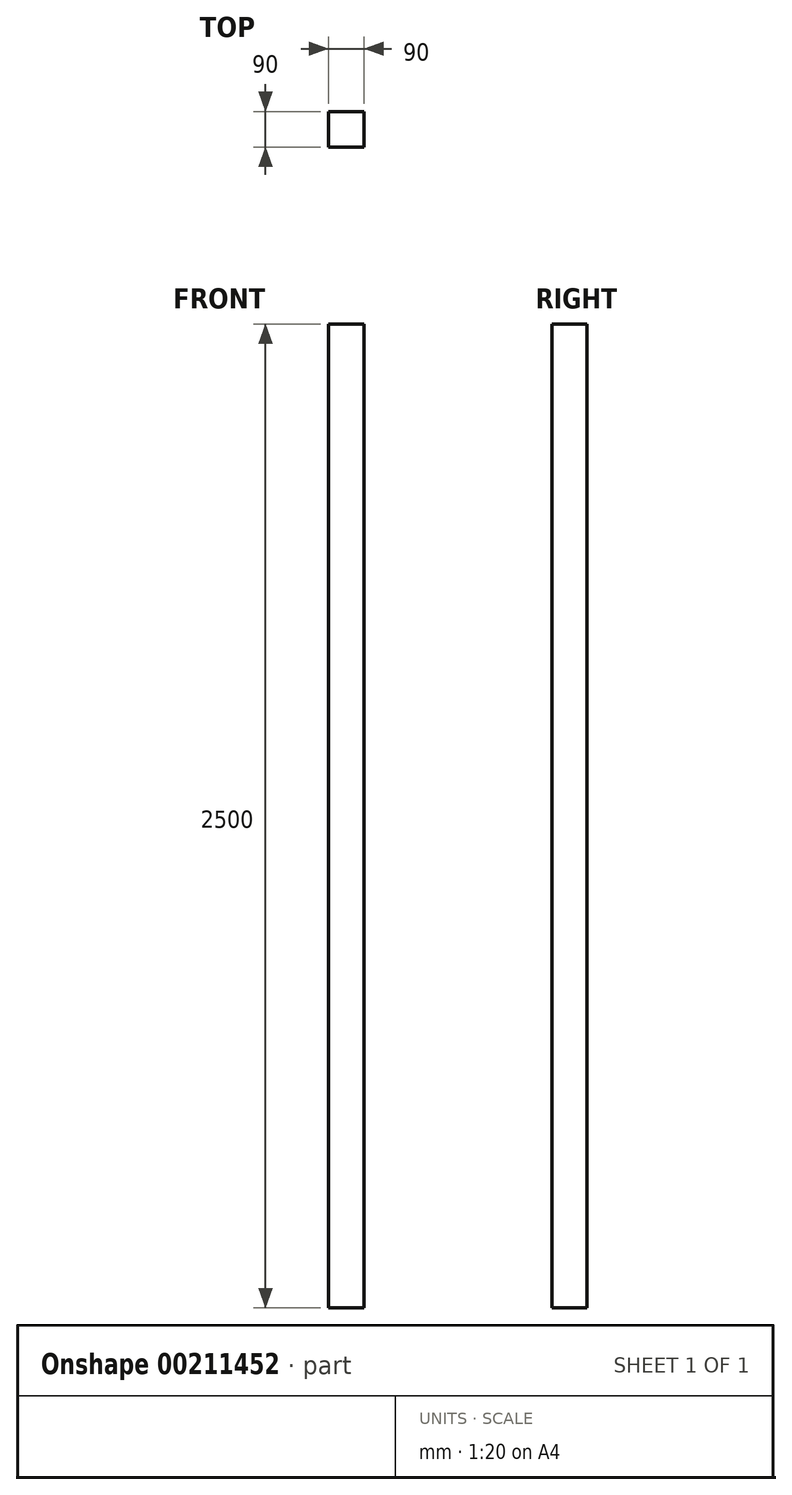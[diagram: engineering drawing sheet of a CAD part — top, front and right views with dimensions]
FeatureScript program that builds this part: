
annotation { "Feature Type Name" : "Feature", "Feature Type Description" : "" }
export const myFeature = defineFeature(function(context is Context, id is Id, definition is map)
    precondition{}
    {
        {
            var Q0;
            Q0=qCreatedBy(makeId("Top.planeOp"),FACE);
            var sketch = newSketch(context, id + "F0", { "sketchPlane" : qUnion([Q0])});
            skLineSegment(sketch, "E0.bottom", {"start": v(45, 45) * mm, "end": v(-45, 45) * mm});
            skLineSegment(sketch, "E0.top", {"start": v(45, -45) * mm, "end": v(-45, -45) * mm});
            skLineSegment(sketch, "E0.left", {"start": v(45, 45) * mm, "end": v(45, -45) * mm});
            skLineSegment(sketch, "E0.right", {"start": v(-45, 45) * mm, "end": v(-45, -45) * mm});
            skPoint(sketch, "E0.middle", {"position": v(0, 0) * mm});
            skSolve(sketch);
        }
        {
            var Q0;
            Q0 = qSketchRegion(id + "F0", true);
            extrude(context, id + "F1", {"entities" : qUnion([Q0]), "depth" : 2500 * mm, "symmetric" : true});
        }
    });
